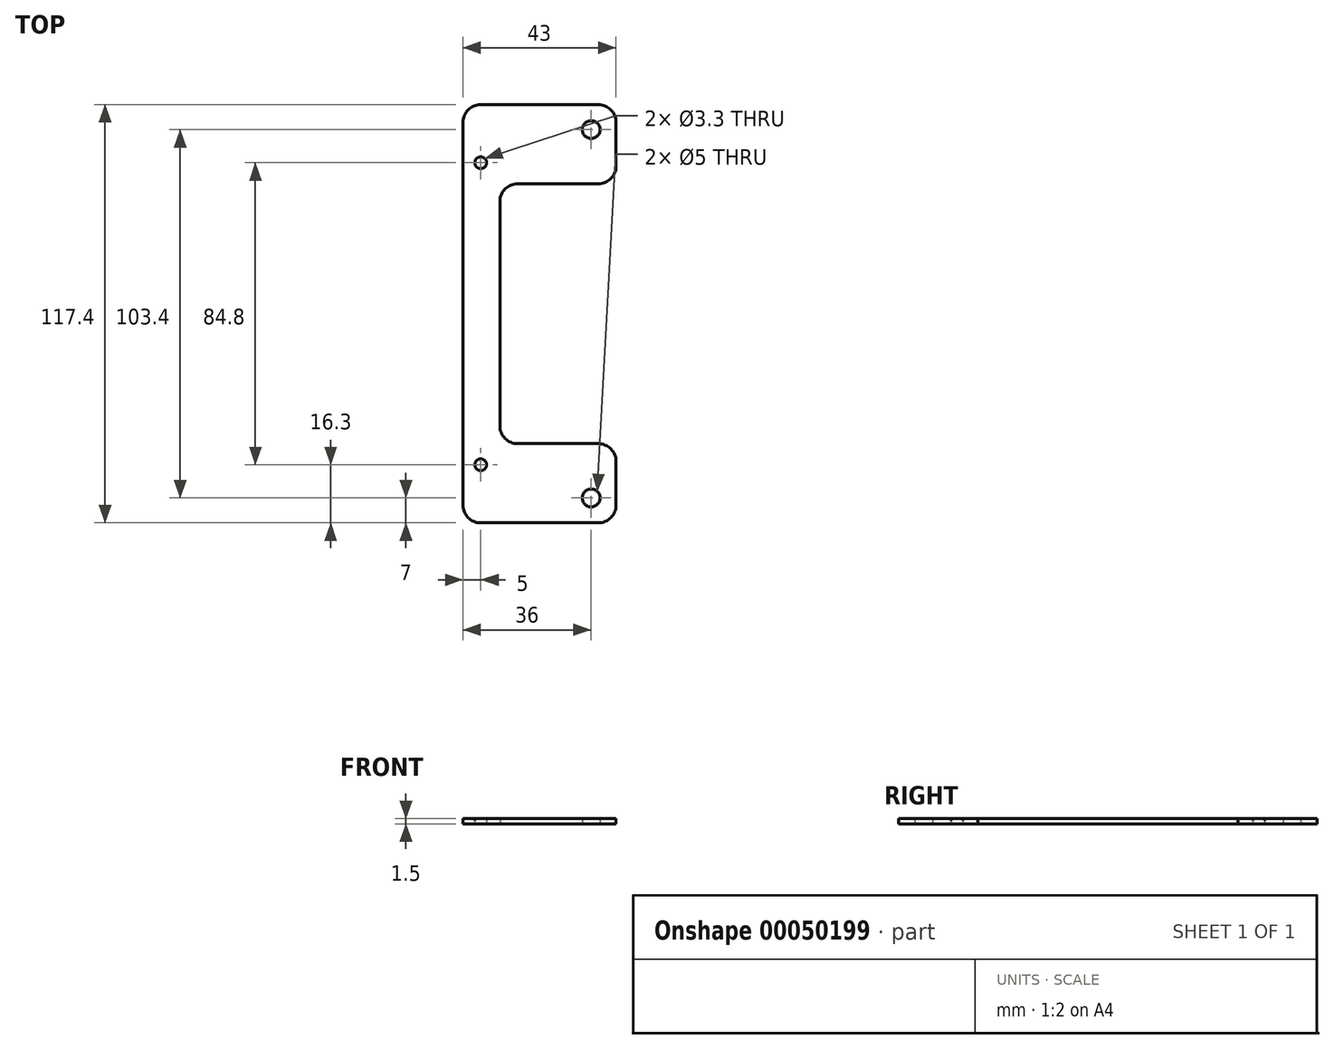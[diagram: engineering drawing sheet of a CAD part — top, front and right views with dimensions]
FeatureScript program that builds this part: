
annotation { "Feature Type Name" : "Feature", "Feature Type Description" : "" }
export const myFeature = defineFeature(function(context is Context, id is Id, definition is map)
    precondition{}
    {
        {
            var Q0;
            Q0=qCreatedBy(makeId("Top.planeOp"),FACE);
            var sketch = newSketch(context, id + "F0", { "sketchPlane" : qUnion([Q0])});
            skLineSegment(sketch, "E0.bottom", {"start": v(-30.61, 0) * mm, "end": v(-41, 0) * mm});
            skLineSegment(sketch, "E0.top", {"start": v(-3, 58.7) * mm, "end": v(-36, 58.7) * mm});
            skLineSegment(sketch, "E0.left", {"start": v(2, 41.48) * mm, "end": v(2, 53.7) * mm});
            skLineSegment(sketch, "E0.right", {"start": v(-41, 0) * mm, "end": v(-41, 53.7) * mm});
            skCircle(sketch, "E1", {"center": v(-36, 42.4) * mm, "radius": 1.65 * mm});
            skCircle(sketch, "E2", {"center": v(-5, 51.7) * mm, "radius": 2.5 * mm});
            skLineSegment(sketch, "E3", {"start": v(-5, 51.7) * mm, "end": v(-5, 59.66) * mm, "construction": true});
            skLineSegment(sketch, "E4", {"start": v(-5, 59.66) * mm, "end": v(-5, 20.33) * mm, "construction": true});
            skLineSegment(sketch, "E5", {"start": v(-5, 51.7) * mm, "end": v(-27.85, 51.7) * mm, "construction": true});
            skLineSegment(sketch, "E6", {"start": v(-3, 36.48) * mm, "end": v(-25.61, 36.48) * mm});
            skLineSegment(sketch, "E7", {"start": v(-30.61, 31.48) * mm, "end": v(-30.61, 0) * mm});
            skLineSegment(sketch, "E8.MirrorCS", {"start": v(-5, -51.7) * mm, "end": v(-5, -59.66) * mm, "construction": true});
            skLineSegment(sketch, "E9.MirrorCS", {"start": v(-41, 0) * mm, "end": v(-41, -53.7) * mm});
            skLineSegment(sketch, "E10.MirrorCS", {"start": v(2, -41.48) * mm, "end": v(2, -53.7) * mm});
            skCircle(sketch, "E11.MirrorC", {"center": v(-36, -42.4) * mm, "radius": 1.65 * mm});
            skLineSegment(sketch, "E12.MirrorCS", {"start": v(-3, -58.7) * mm, "end": v(-36, -58.7) * mm});
            skCircle(sketch, "E13.MirrorC", {"center": v(-5, -51.7) * mm, "radius": 2.5 * mm});
            skLineSegment(sketch, "E14.MirrorCS", {"start": v(-5, -51.7) * mm, "end": v(-27.85, -51.7) * mm, "construction": true});
            skLineSegment(sketch, "E15.MirrorCS", {"start": v(-5, -59.66) * mm, "end": v(-5, -20.33) * mm, "construction": true});
            skLineSegment(sketch, "E16.MirrorCS", {"start": v(-3, -36.48) * mm, "end": v(-25.61, -36.48) * mm});
            skLineSegment(sketch, "E17.MirrorCS", {"start": v(-30.61, -31.48) * mm, "end": v(-30.61, 0) * mm});
            skPoint(sketch, "E18.visualSharp", {"position": v(2, 58.7) * mm});
            skArc(sketch, "E18.filletArc", {"start": v(2, 53.7) * mm, "mid": v(0.54, 57.24) * mm, "end": v(-3, 58.7) * mm});
            skPoint(sketch, "E19.visualSharp", {"position": v(2, 36.48) * mm});
            skArc(sketch, "E19.filletArc", {"start": v(-3, 36.48) * mm, "mid": v(0.54, 37.94) * mm, "end": v(2, 41.48) * mm});
            skPoint(sketch, "E20.visualSharp", {"position": v(-41, 58.7) * mm});
            skArc(sketch, "E20.filletArc", {"start": v(-36, 58.7) * mm, "mid": v(-39.54, 57.24) * mm, "end": v(-41, 53.7) * mm});
            skPoint(sketch, "E21.visualSharp", {"position": v(2, -36.48) * mm});
            skArc(sketch, "E21.filletArc", {"start": v(2, -41.48) * mm, "mid": v(0.54, -37.94) * mm, "end": v(-3, -36.48) * mm});
            skPoint(sketch, "E22.visualSharp", {"position": v(-41, -58.7) * mm});
            skArc(sketch, "E22.filletArc", {"start": v(-41, -53.7) * mm, "mid": v(-39.54, -57.24) * mm, "end": v(-36, -58.7) * mm});
            skPoint(sketch, "E23.visualSharp", {"position": v(2, -58.7) * mm});
            skArc(sketch, "E23.filletArc", {"start": v(-3, -58.7) * mm, "mid": v(0.54, -57.24) * mm, "end": v(2, -53.7) * mm});
            skPoint(sketch, "E24.visualSharp", {"position": v(-30.61, 36.48) * mm});
            skArc(sketch, "E24.filletArc", {"start": v(-25.61, 36.48) * mm, "mid": v(-29.15, 35.02) * mm, "end": v(-30.61, 31.48) * mm});
            skPoint(sketch, "E25.visualSharp", {"position": v(-30.61, -36.48) * mm});
            skArc(sketch, "E25.filletArc", {"start": v(-30.61, -31.48) * mm, "mid": v(-29.15, -35.02) * mm, "end": v(-25.61, -36.48) * mm});
            skSolve(sketch);
        }
        {
            var Q0;
            Q0 = qSketchRegion(id + "F0", true);
            extrude(context, id + "F1", {"entities" : qUnion([Q0]), "depth" : 1.5 * mm});
        }
        {
            var Q0;
            Q0=makeQuery(id+"F1.opExtrude","CAP_EDGE",EDGE,{"disambiguationData":[OSD([sQuery(id+"F0.wireOp",EDGE,"E1")])],"isStart":false});
            var Q1;
            Q1=makeQuery(id+"F1.opExtrude","CAP_EDGE",EDGE,{"disambiguationData":[OSD([sQuery(id+"F0.wireOp",EDGE,"E11.MirrorC")])],"isStart":false});
            fillet(context, id + "F2", {"entities" : qUnion([Q0, Q1]), "radius" : 0.5 * mm, "tangentPropagation" : true, "allowEdgeOverflow" : false});
        }
    });
